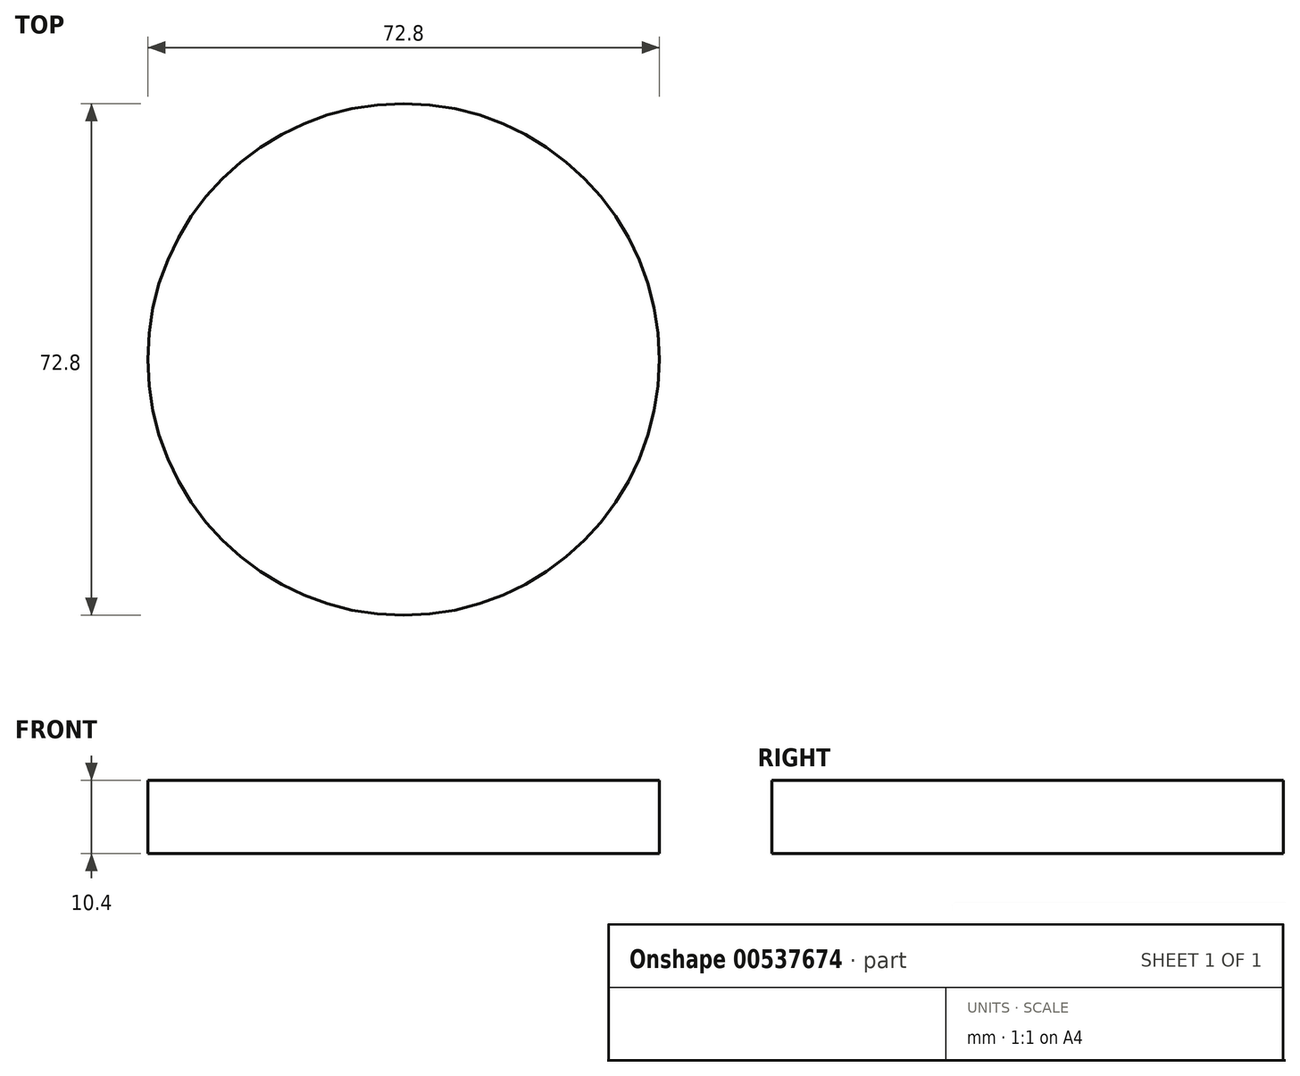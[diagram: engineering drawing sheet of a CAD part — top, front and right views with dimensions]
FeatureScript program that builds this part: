
annotation { "Feature Type Name" : "Feature", "Feature Type Description" : "" }
export const myFeature = defineFeature(function(context is Context, id is Id, definition is map)
    precondition{}
    {
        {
            var Q0;
            Q0=qCreatedBy(makeId("Top.planeOp"),FACE);
            var sketch = newSketch(context, id + "F0", { "sketchPlane" : qUnion([Q0])});
            skCircle(sketch, "E0", {"center": v(0, 0) * mm, "radius": 36.4 * mm});
            skSolve(sketch);
        }
        {
            var Q0;
            Q0 = qSketchRegion(id + "F0", true);
            extrude(context, id + "F1", {"entities" : qUnion([Q0]), "oppositeDirection" : true, "depth" : 10.4 * mm, "offsetDistance" : 25 * mm});
        }
    });
